# Revit family: RN 23100 Valvola diritta
name_source: partatom
category: Rohrzubehör
units: mm (PartAtom-declared; Revit-internal decimal feet)

## family parameters
Arbeitsebenenbasiert = Nein
Beim Laden mit Abzugskörper schneiden = Nein
Bemaßung runder Anschluss = Durchmesser verwenden
Gemeinsam genutzt = Nein
Immer vertikal = Ja
Teiletyp = Ventil - Zerlegung in

## types (8) — shared parameters
1.010.00.2 Blattnummer der Richtlinie = 17
1.010.00.3 Ausgabedatum (Monat) der Richtlinie = 201601
1.010.00.4 Herstellername = R. Nussbaum AG
1.010.00.5 Revisionsdatum der Datei = 20190528
1.010.00.6 Webadresse des Herstellers = http://www.nussbaum.ch
1.100.00.3 Sortiernummer für Anzeigereihenfolge = 1
1.100.00.4 Produktbezeichnung = Absperrarmaturen
1.960/3L.00.8 Link (URL) = https://www.nussbaum.ch
17.700.00.4 Armaturentyp = 1
17.700.00.7 Maximale Betriebstemperatur TB [°C] = 90
17.700.00.8 Maximaler Betriebsdruck (Arbeitsdruck) ps [1.0 · 105 Pa] = 16
Connector Visibility = Nein
EnclosingSpace Visibility = Nein
Hersteller = R. Nussbauzm AG
URL = https://www.nussbaum.ch

## per-type parameters (varying)
- DN 65: 1.800.00.3 TGA-Nummer=001047???0000000000000000000020070000000000000000100000000; 1.810.00.3 Hersteller-Bestellnummer=23100.1; 1.810.00.4 DATANORM-Nummer=23100.1; 1.810.00.5 StLB-Nummer=623.121; 1.810.00.6 GTIN-Nummer=7612945726193; 17.700.00.30 Produktbeschreibung=23100.10, Geradsitzventil, DN=65, Rp=2½; 17.700.00.5 Nennweite DN=65; 17.700.00.6 kvs-Wert [m3/h]=55.59; CONNECTOR0_DIAMETER_dX_0r=65 mm; CONNECTOR0_dX_00=80 mm; CONNECTOR0_dX_01=64 mm; CONNECTOR0_ref_dX=64 mm; CONNECTOR1_DIAMETER_dX_0r=65 mm; CONNECTOR1_dX_00=64 mm; CONNECTOR1_dX_01=80 mm; CONNECTOR1_ref_dX=64 mm; Modell=23100.1; R. Nussbaum AG 23100.03 de Visibility=Nein; R. Nussbaum AG 23100.04 de Visibility=Nein; R. Nussbaum AG 23100.05 de Visibility=Nein; R. Nussbaum AG 23100.06 de Visibility=Nein; R. Nussbaum AG 23100.07 de Visibility=Nein; R. Nussbaum AG 23100.08 de Visibility=Nein; R. Nussbaum AG 23100.09 de Visibility=Nein; R. Nussbaum AG 23100.10 de Visibility=Ja; Typenkommentare=Valvola dirittaDN 65
- DN 10: 1.800.00.3 TGA-Nummer=001047???0000000000000000000020070000000000000000200000000; 1.810.00.3 Hersteller-Bestellnummer=23100.03; 1.810.00.4 DATANORM-Nummer=23100.03; 1.810.00.5 StLB-Nummer=623.112; 1.810.00.6 GTIN-Nummer=7612945731760; 17.700.00.30 Produktbeschreibung=23100.03, Geradsitzventil, DN=10, Rp=3/8; 17.700.00.5 Nennweite DN=10; 17.700.00.6 kvs-Wert [m3/h]=2.52; CONNECTOR0_DIAMETER_dX_0r=12 mm  [stored 0.0393701 ft]; CONNECTOR0_dX_00=30 mm; CONNECTOR0_dX_01=20 mm; CONNECTOR0_ref_dX=20 mm; CONNECTOR1_DIAMETER_dX_0r=12 mm  [stored 0.0393701 ft]; CONNECTOR1_dX_00=20 mm; CONNECTOR1_dX_01=30 mm; CONNECTOR1_ref_dX=20 mm; Modell=23100.03; R. Nussbaum AG 23100.03 de Visibility=Ja; R. Nussbaum AG 23100.04 de Visibility=Nein; R. Nussbaum AG 23100.05 de Visibility=Nein; R. Nussbaum AG 23100.06 de Visibility=Nein; R. Nussbaum AG 23100.07 de Visibility=Nein; R. Nussbaum AG 23100.08 de Visibility=Nein; R. Nussbaum AG 23100.09 de Visibility=Nein; R. Nussbaum AG 23100.10 de Visibility=Nein; Typenkommentare=Valvola dirittaDN 10
- DN 15: 1.800.00.3 TGA-Nummer=001047???0000000000000000000020070000000000000000300000000; 1.810.00.3 Hersteller-Bestellnummer=23100.04; 1.810.00.4 DATANORM-Nummer=23100.04; 1.810.00.5 StLB-Nummer=623.113; 1.810.00.6 GTIN-Nummer=7612945731777; 17.700.00.30 Produktbeschreibung=23100.04, Geradsitzventil, DN=15, Rp=½; 17.700.00.5 Nennweite DN=15; 17.700.00.6 kvs-Wert [m3/h]=3.61; CONNECTOR0_DIAMETER_dX_0r=15 mm  [stored 0.0492126 ft]; CONNECTOR0_dX_00=30 mm; CONNECTOR0_dX_01=17 mm; CONNECTOR0_ref_dX=17 mm; CONNECTOR1_DIAMETER_dX_0r=15 mm  [stored 0.0492126 ft]; CONNECTOR1_dX_00=17 mm; CONNECTOR1_dX_01=30 mm; CONNECTOR1_ref_dX=17 mm; Modell=23100.04; R. Nussbaum AG 23100.03 de Visibility=Nein; R. Nussbaum AG 23100.04 de Visibility=Ja; R. Nussbaum AG 23100.05 de Visibility=Nein; R. Nussbaum AG 23100.06 de Visibility=Nein; R. Nussbaum AG 23100.07 de Visibility=Nein; R. Nussbaum AG 23100.08 de Visibility=Nein; R. Nussbaum AG 23100.09 de Visibility=Nein; R. Nussbaum AG 23100.10 de Visibility=Nein; Typenkommentare=Valvola dirittaDN 15
- DN 20: 1.800.00.3 TGA-Nummer=001047???0000000000000000000020070000000000000000400000000; 1.810.00.3 Hersteller-Bestellnummer=23100.05; 1.810.00.4 DATANORM-Nummer=23100.05; 1.810.00.5 StLB-Nummer=623.114; 1.810.00.6 GTIN-Nummer=7612945731784; 17.700.00.30 Produktbeschreibung=23100.05, Geradsitzventil, DN=20, Rp=¾; 17.700.00.5 Nennweite DN=20; 17.700.00.6 kvs-Wert [m3/h]=5.86; CONNECTOR0_DIAMETER_dX_0r=20 mm; CONNECTOR0_dX_00=38 mm; CONNECTOR0_dX_01=23 mm; CONNECTOR0_ref_dX=23 mm; CONNECTOR1_DIAMETER_dX_0r=20 mm; CONNECTOR1_dX_00=23 mm; CONNECTOR1_dX_01=38 mm; CONNECTOR1_ref_dX=23 mm; Modell=23100.05; R. Nussbaum AG 23100.03 de Visibility=Nein; R. Nussbaum AG 23100.04 de Visibility=Nein; R. Nussbaum AG 23100.05 de Visibility=Ja; R. Nussbaum AG 23100.06 de Visibility=Nein; R. Nussbaum AG 23100.07 de Visibility=Nein; R. Nussbaum AG 23100.08 de Visibility=Nein; R. Nussbaum AG 23100.09 de Visibility=Nein; R. Nussbaum AG 23100.10 de Visibility=Nein; Typenkommentare=Valvola dirittaDN 20
- DN 25: 1.800.00.3 TGA-Nummer=001047???0000000000000000000020070000000000000000500000000; 1.810.00.3 Hersteller-Bestellnummer=23100.06; 1.810.00.4 DATANORM-Nummer=23100.06; 1.810.00.5 StLB-Nummer=623.115; 1.810.00.6 GTIN-Nummer=7612945728623; 17.700.00.30 Produktbeschreibung=23100.06, Geradsitzventil, DN=25, Rp=1; 17.700.00.5 Nennweite DN=25; 17.700.00.6 kvs-Wert [m3/h]=9.41; CONNECTOR0_DIAMETER_dX_0r=25 mm  [stored 0.082021 ft]; CONNECTOR0_dX_00=45 mm; CONNECTOR0_dX_01=28 mm; CONNECTOR0_ref_dX=28 mm; CONNECTOR1_DIAMETER_dX_0r=25 mm  [stored 0.082021 ft]; CONNECTOR1_dX_00=28 mm; CONNECTOR1_dX_01=45 mm; CONNECTOR1_ref_dX=28 mm; Modell=23100.06; R. Nussbaum AG 23100.03 de Visibility=Nein; R. Nussbaum AG 23100.04 de Visibility=Nein; R. Nussbaum AG 23100.05 de Visibility=Nein; R. Nussbaum AG 23100.06 de Visibility=Ja; R. Nussbaum AG 23100.07 de Visibility=Nein; R. Nussbaum AG 23100.08 de Visibility=Nein; R. Nussbaum AG 23100.09 de Visibility=Nein; R. Nussbaum AG 23100.10 de Visibility=Nein; Typenkommentare=Valvola dirittaDN 25
- DN 32: 1.800.00.3 TGA-Nummer=001047???0000000000000000000020070000000000000000600000000; 1.810.00.3 Hersteller-Bestellnummer=23100.07; 1.810.00.4 DATANORM-Nummer=23100.07; 1.810.00.5 StLB-Nummer=623.116; 1.810.00.6 GTIN-Nummer=7612945728630; 17.700.00.30 Produktbeschreibung=23100.07, Geradsitzventil, DN=32, Rp=1¼; 17.700.00.5 Nennweite DN=32; 17.700.00.6 kvs-Wert [m3/h]=16.13; CONNECTOR0_DIAMETER_dX_0r=32 mm; CONNECTOR0_dX_00=53 mm; CONNECTOR0_dX_01=34 mm; CONNECTOR0_ref_dX=34 mm; CONNECTOR1_DIAMETER_dX_0r=32 mm; CONNECTOR1_dX_00=34 mm; CONNECTOR1_dX_01=53 mm; CONNECTOR1_ref_dX=34 mm; Modell=23100.07; R. Nussbaum AG 23100.03 de Visibility=Nein; R. Nussbaum AG 23100.04 de Visibility=Nein; R. Nussbaum AG 23100.05 de Visibility=Nein; R. Nussbaum AG 23100.06 de Visibility=Nein; R. Nussbaum AG 23100.07 de Visibility=Ja; R. Nussbaum AG 23100.08 de Visibility=Nein; R. Nussbaum AG 23100.09 de Visibility=Nein; R. Nussbaum AG 23100.10 de Visibility=Nein; Typenkommentare=Valvola dirittaDN 32
- DN 40: 1.800.00.3 TGA-Nummer=001047???0000000000000000000020070000000000000000700000000; 1.810.00.3 Hersteller-Bestellnummer=23100.08; 1.810.00.4 DATANORM-Nummer=23100.08; 1.810.00.5 StLB-Nummer=623.117; 1.810.00.6 GTIN-Nummer=7612945726803; 17.700.00.30 Produktbeschreibung=23100.08, Geradsitzventil, DN=40, Rp=1½; 17.700.00.5 Nennweite DN=40; 17.700.00.6 kvs-Wert [m3/h]=22.01; CONNECTOR0_DIAMETER_dX_0r=40 mm; CONNECTOR0_dX_00=60 mm; CONNECTOR0_dX_01=41 mm; CONNECTOR0_ref_dX=41 mm; CONNECTOR1_DIAMETER_dX_0r=40 mm; CONNECTOR1_dX_00=41 mm; CONNECTOR1_dX_01=60 mm; CONNECTOR1_ref_dX=41 mm; Modell=23100.08; R. Nussbaum AG 23100.03 de Visibility=Nein; R. Nussbaum AG 23100.04 de Visibility=Nein; R. Nussbaum AG 23100.05 de Visibility=Nein; R. Nussbaum AG 23100.06 de Visibility=Nein; R. Nussbaum AG 23100.07 de Visibility=Nein; R. Nussbaum AG 23100.08 de Visibility=Ja; R. Nussbaum AG 23100.09 de Visibility=Nein; R. Nussbaum AG 23100.10 de Visibility=Nein; Typenkommentare=Valvola dirittaDN 40
- DN 50: 1.800.00.3 TGA-Nummer=001047???0000000000000000000020070000000000000000800000000; 1.810.00.3 Hersteller-Bestellnummer=23100.09; 1.810.00.4 DATANORM-Nummer=23100.09; 1.810.00.5 StLB-Nummer=623.118; 1.810.00.6 GTIN-Nummer=7612945726810; 17.700.00.30 Produktbeschreibung=23100.09, Geradsitzventil, DN=50, Rp=2; 17.700.00.5 Nennweite DN=50; 17.700.00.6 kvs-Wert [m3/h]=35.29; CONNECTOR0_DIAMETER_dX_0r=50 mm; CONNECTOR0_dX_00=70 mm; CONNECTOR0_dX_01=46 mm; CONNECTOR0_ref_dX=46 mm; CONNECTOR1_DIAMETER_dX_0r=50 mm; CONNECTOR1_dX_00=46 mm; CONNECTOR1_dX_01=70 mm; CONNECTOR1_ref_dX=46 mm; Modell=23100.09; R. Nussbaum AG 23100.03 de Visibility=Nein; R. Nussbaum AG 23100.04 de Visibility=Nein; R. Nussbaum AG 23100.05 de Visibility=Nein; R. Nussbaum AG 23100.06 de Visibility=Nein; R. Nussbaum AG 23100.07 de Visibility=Nein; R. Nussbaum AG 23100.08 de Visibility=Nein; R. Nussbaum AG 23100.09 de Visibility=Ja; R. Nussbaum AG 23100.10 de Visibility=Nein; Typenkommentare=Valvola dirittaDN 50

note: [stored X ft] marks values corroborated as IEEE doubles in the binary element streams (Revit-internal decimal feet)

## geometry (parser evidence)
native form markers: Sweep x1
no freeform markers — native parametric forms only
